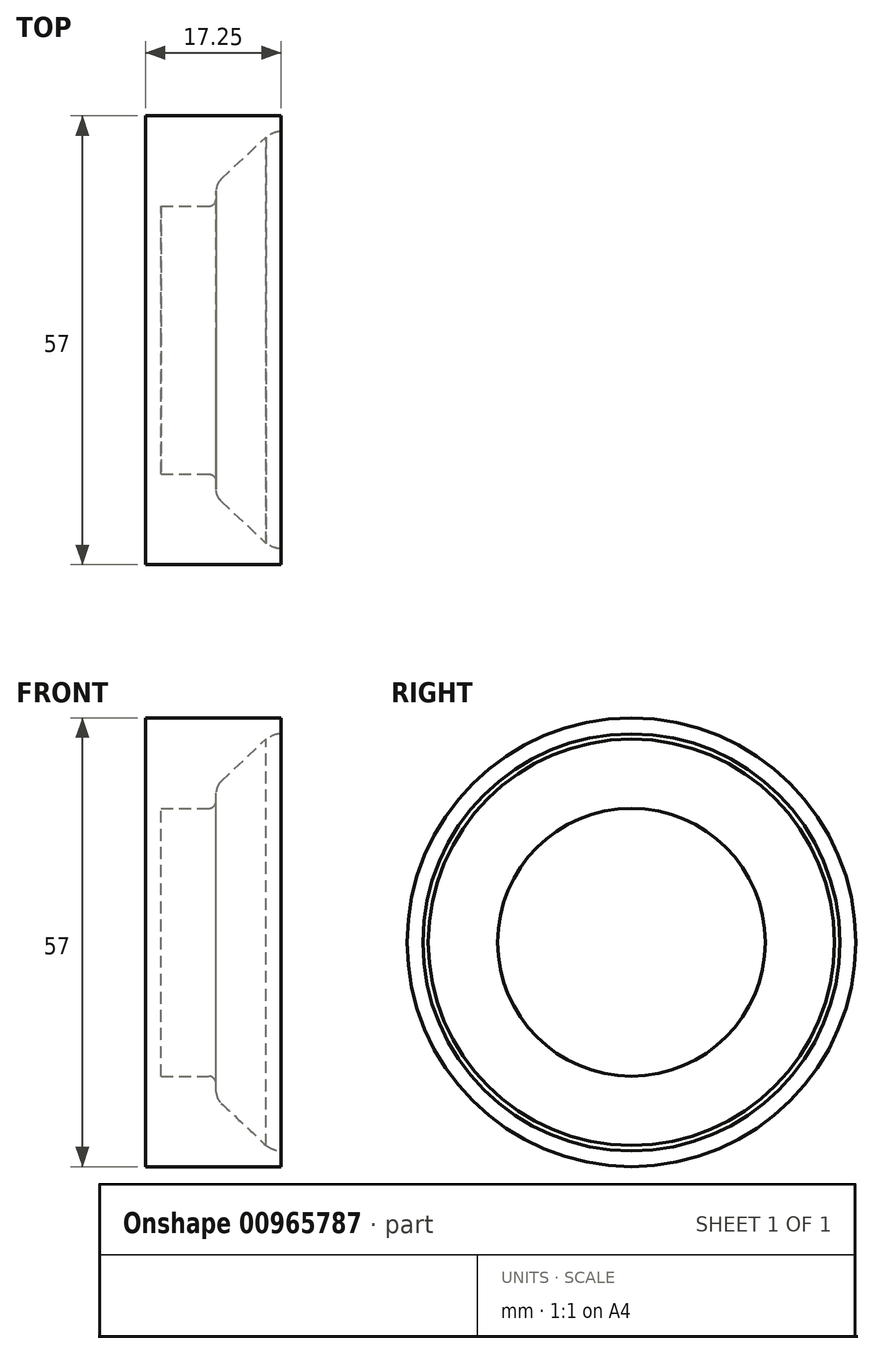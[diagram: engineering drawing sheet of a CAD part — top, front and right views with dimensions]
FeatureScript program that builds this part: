
annotation { "Feature Type Name" : "Feature", "Feature Type Description" : "" }
export const myFeature = defineFeature(function(context is Context, id is Id, definition is map)
    precondition{}
    {
        {
            var Q0;
            Q0=qCreatedBy(makeId("Front.planeOp"),FACE);
            var sketch = newSketch(context, id + "F0", { "sketchPlane" : qUnion([Q0])});
            skFitSpline(sketch, "E0", {"points": [v(12.84, 25.48) * mm, v(14.4, 26.36) * mm, v(15.9, 26.46) * mm, v(17.5, 25.94) * mm, v(18.63, 25.07) * mm, v(18.87, 24.79) * mm], "startDerivative": vector(6.57, 4.44) * mm, "endDerivative": vector(1.73, -2.25) * mm});
            skPoint(sketch, "E1.visualSharp", {"position": v(7, 16) * mm});
            skLineSegment(sketch, "E2", {"start": v(7.63, 20.43) * mm, "end": v(13.36, 25.83) * mm});
            skPoint(sketch, "E3.visualSharp", {"position": v(7, 19.84) * mm});
            skArc(sketch, "E3.filletArc", {"start": v(7.63, 20.43) * mm, "mid": v(7.16, 19.77) * mm, "end": v(7, 18.97) * mm});
            skLineSegment(sketch, "E4", {"start": v(0, 0) * mm, "end": v(0, 17) * mm});
            skLineSegment(sketch, "E5", {"start": v(7, 18) * mm, "end": v(7, 18.97) * mm});
            skPoint(sketch, "E6.visualSharp", {"position": v(7, 17) * mm});
            skLineSegment(sketch, "E7", {"start": v(0, 17) * mm, "end": v(6, 17) * mm});
            skArc(sketch, "E8.filletArc", {"start": v(6, 17) * mm, "mid": v(6.7, 17.3) * mm, "end": v(7, 18) * mm});
            skLineSegment(sketch, "E9", {"start": v(15.25, 26.5) * mm, "end": v(15.25, 28.5) * mm});
            skLineSegment(sketch, "E10", {"start": v(0, 0) * mm, "end": v(-2, 0) * mm});
            skLineSegment(sketch, "E11", {"start": v(-2, 0) * mm, "end": v(-2, 28.5) * mm});
            skLineSegment(sketch, "E12", {"start": v(-2, 28.5) * mm, "end": v(15.25, 28.5) * mm});
            skSolve(sketch);
        }
        {
            var Q0;
            {var subQ0=sQuery(id+"F0.wireOp",EDGE,"E0");Q0=makeQuery(id+"F0.imprint","IMPRINT",FACE,{"disambiguationData":[TD([[makeQuery(id+"F0.imprint","IMPRINT",EDGE,{"derivedFrom":subQ0}),1.0]])]});}
            var Q1;
            Q1=sQuery(id+"F0.wireOp",EDGE,"E10");
            revolve(context, id + "F1", {"surfaceOperationType" : NewSurfaceOperationType.NEW, "entities" : qUnion([Q0]), "axis" : qUnion([Q1]), "revolveType" : RevolveType.FULL});
        }
    });
